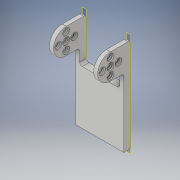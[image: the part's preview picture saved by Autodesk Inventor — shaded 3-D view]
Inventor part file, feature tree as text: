
AUTODESK INVENTOR PART (.ipt)
format: ipt  version: 2018 (Build 220112000, 112)  size: 240,128 bytes
history: native  units: in
note: dims shown in document units (in); Inventor stores cm internally (conversion verified against a paired STEP export)
features: extrude x5, sketch x5, chamfer x2, plane x2, pattern_linear x2, mirror x1, fillet x1
ambient origin geometry x8: Origin, YZ Plane, XZ Plane, XY Plane, X Axis, Y Axis, Z Axis, Center Point
bodies: Solid1 (feature_tree)
feature tree (18):
  extrude  "Extrusion1"  Depth=0.1969in
  extrude  "Extrusion2"  Depth=0.0787in
  extrude  "Extrusion3"  Depth=0.0787in
  extrude  "Extrusion4"  Depth=0.1181in
  chamfer  "Chamfer1"  Distance=0.1181in
  chamfer  "Chamfer2"  Distance=0.0394in
  plane  "Work Plane1"
  pattern_linear  "Rectangular Pattern1"  Spacing1=0.2047in  [1 undecoded]
  pattern_linear  "Rectangular Pattern2"  Spacing1=0.0394in  [1 undecoded]
  extrude  "Extrusion5"  Depth=0.0787in TaperAngle=45.0deg
  mirror  "Mirror1"
  fillet  "Fillet1"  Radius=0.0787in
  sketch  "Sketch1"  dims[d0=0.748in d4=0.1969in]
  sketch  "Sketch2"  dims[d6=2.185in d8=0.0787in]
  sketch  "Sketch3"  dims[d9=0.0787in d10=0.0787in]
  sketch  "Sketch4"  dims[d11=0.1181in d12=0.0in d13=0.1614in d14=0.1181in d15=0.0in]
  sketch  "Sketch5"  dims[d16=0.2047in d17=0.0394in d18=0.0in d19=0.2047in d20=0.0394in d21=0.0in d22=0.0217in d23=0.0787in d24=45.0deg d25=0.0217in d26=0.0787in d27=45.0deg d28=0.7874in d30=0.2362in d31=0.7874in d33=0.2362in d34=0.7874in d36=0.2362in d37=0.7874in d39=0.2362in d40=1.5748in d41=0.0787in d42=0.5906in d43=0.0in d44=0.0787in]
  plane  "Work Plane2"
note: 2 required parameter values undecoded (feature->parameter linkage not recoverable at this tier; creation-order binding heuristic only, values carry confidence <= 0.55)
